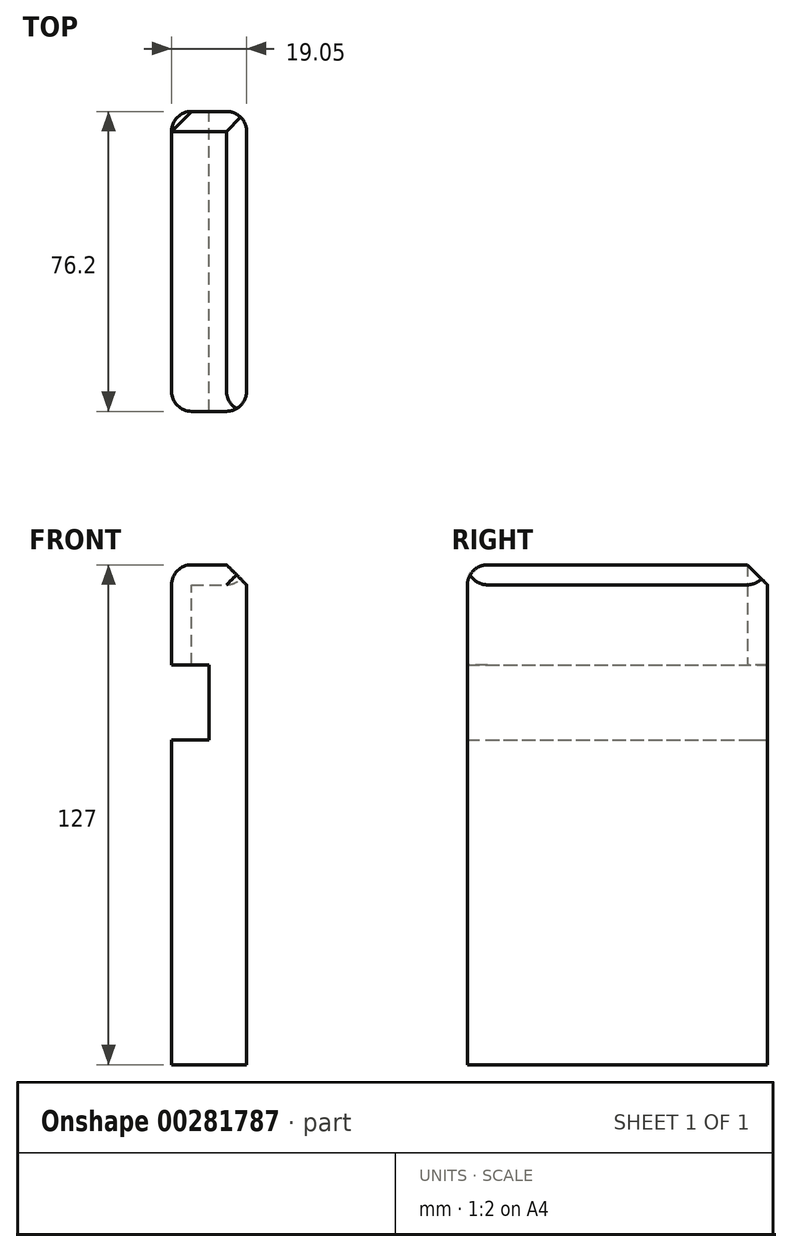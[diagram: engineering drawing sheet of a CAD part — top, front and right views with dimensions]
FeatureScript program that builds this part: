
annotation { "Feature Type Name" : "Feature", "Feature Type Description" : "" }
export const myFeature = defineFeature(function(context is Context, id is Id, definition is map)
    precondition{}
    {
        {
            var Q0;
            Q0=qCreatedBy(makeId("Front.planeOp"),FACE);
            var sketch = newSketch(context, id + "F0", { "sketchPlane" : qUnion([Q0])});
            skLineSegment(sketch, "E0", {"start": v(0, 0) * mm, "end": v(0, 127) * mm});
            skLineSegment(sketch, "E1", {"start": v(0, 127) * mm, "end": v(-19.05, 127) * mm});
            skLineSegment(sketch, "E2", {"start": v(-19.05, 127) * mm, "end": v(-19.05, 101.6) * mm});
            skLineSegment(sketch, "E3", {"start": v(-19.05, 101.6) * mm, "end": v(-9.52, 101.6) * mm});
            skLineSegment(sketch, "E4", {"start": v(-9.52, 101.6) * mm, "end": v(-9.52, 82.55) * mm});
            skLineSegment(sketch, "E5", {"start": v(-9.52, 82.55) * mm, "end": v(-19.05, 82.55) * mm});
            skLineSegment(sketch, "E6", {"start": v(-19.05, 82.55) * mm, "end": v(-19.05, 0) * mm});
            skLineSegment(sketch, "E7", {"start": v(-19.05, 0) * mm, "end": v(0, 0) * mm});
            skSolve(sketch);
        }
        {
            var Q0;
            Q0 = qSketchRegion(id + "F0", true);
            extrude(context, id + "F1", {"entities" : qUnion([Q0]), "depth" : 76.2 * mm});
        }
        {
            var Q0;
            Q0=makeQuery(id+"F1.opExtrude","SWEPT_EDGE",EDGE,{"disambiguationData":[OSD([sQuery(id+"F0.wireOp",EDGE,"E0"),sQuery(id+"F0.wireOp",EDGE,"E1")])]});
            chamfer(context, id + "F2", {"entities" : qUnion([Q0]), "width" : 5.08 * mm, "tangentPropagation" : true});
        }
        {
            var Q0;
            Q0=makeQuery(id+"F1.opExtrude","SWEPT_EDGE",EDGE,{"disambiguationData":[OSD([sQuery(id+"F0.wireOp",EDGE,"E1"),sQuery(id+"F0.wireOp",EDGE,"E2")])]});
            fillet(context, id + "F3", {"entities" : qUnion([Q0]), "radius" : 5.08 * mm, "tangentPropagation" : true, "allowEdgeOverflow" : false});
        }
        {
            var Q0;
            Q0=makeQuery(id+"F1.opExtrude","CAP_EDGE",EDGE,{"disambiguationData":[OSD([sQuery(id+"F0.wireOp",EDGE,"E1")])],"isStart":false});
            fillet(context, id + "F4", {"entities" : qUnion([Q0]), "radius" : 5.08 * mm, "tangentPropagation" : true, "allowEdgeOverflow" : false});
        }
        {
            var Q0;
            Q0=makeQuery(id+"F1.opExtrude","CAP_EDGE",EDGE,{"disambiguationData":[OSD([sQuery(id+"F0.wireOp",EDGE,"E1")])],"isStart":true});
            chamfer(context, id + "F5", {"entities" : qUnion([Q0]), "width" : 5.08 * mm, "tangentPropagation" : true});
        }
        {
            var Q0;
            Q0=makeQuery(id+"F1.opExtrude","CAP_EDGE",EDGE,{"disambiguationData":[OSD([sQuery(id+"F0.wireOp",EDGE,"E0")])],"isStart":false});
            var Q1;
            Q1=makeQuery(id+"F1.opExtrude","CAP_EDGE",EDGE,{"disambiguationData":[OSD([sQuery(id+"F0.wireOp",EDGE,"E6")])],"isStart":false});
            var Q2;
            Q2=makeQuery(id+"F1.opExtrude","CAP_EDGE",EDGE,{"disambiguationData":[OSD([sQuery(id+"F0.wireOp",EDGE,"E0")])],"isStart":true});
            var Q3;
            Q3=makeQuery(id+"F1.opExtrude","CAP_EDGE",EDGE,{"disambiguationData":[OSD([sQuery(id+"F0.wireOp",EDGE,"E6")])],"isStart":true});
            fillet(context, id + "F6", {"entities" : qUnion([Q0, Q1, Q2, Q3]), "radius" : 5.08 * mm, "tangentPropagation" : true, "allowEdgeOverflow" : false});
        }
    });
